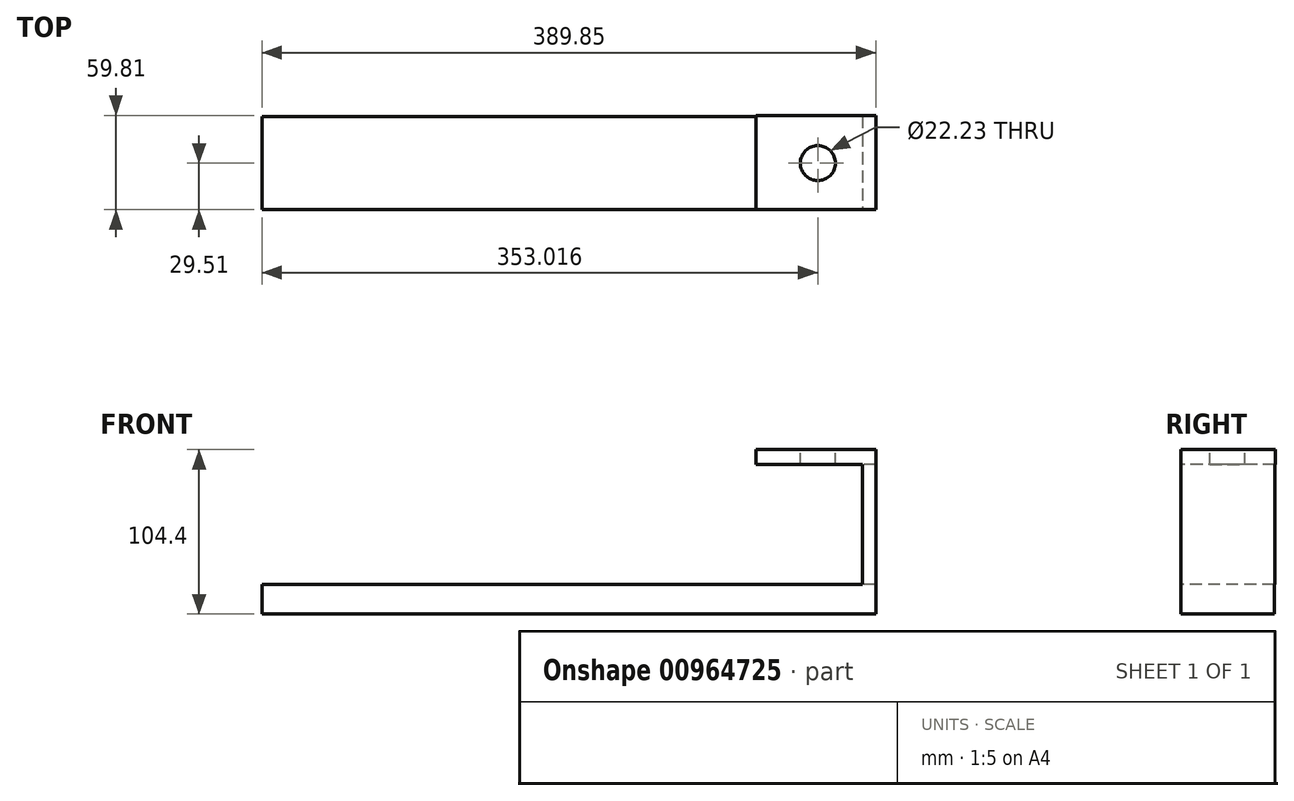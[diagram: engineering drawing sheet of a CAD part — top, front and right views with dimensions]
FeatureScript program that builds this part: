
annotation { "Feature Type Name" : "Feature", "Feature Type Description" : "" }
export const myFeature = defineFeature(function(context is Context, id is Id, definition is map)
    precondition{}
    {
        {
            var Q0;
            Q0=qCreatedBy(makeId("Top.planeOp"),FACE);
            var sketch = newSketch(context, id + "F0", { "sketchPlane" : qUnion([Q0])});
            skLineSegment(sketch, "E0.bottom", {"start": v(62.98, 23.22) * mm, "end": v(-13.26, 23.22) * mm});
            skLineSegment(sketch, "E0.top", {"start": v(62.98, -36.6) * mm, "end": v(-13.26, -36.6) * mm});
            skLineSegment(sketch, "E0.left", {"start": v(62.98, 23.22) * mm, "end": v(62.98, -36.6) * mm});
            skLineSegment(sketch, "E0.right", {"start": v(-13.26, 23.22) * mm, "end": v(-13.26, -36.6) * mm});
            skSolve(sketch);
        }
        {
            var Q0;
            Q0=makeQuery(id+"F0.imprint","IMPRINT",FACE,{"disambiguationData":[TD([[makeQuery(id+"F0.imprint","IMPRINT",EDGE,{"derivedFrom":sQuery(id+"F0.wireOp",EDGE,"E0.bottom")}),1.0]])]});
            extrude(context, id + "F1", {"entities" : qUnion([Q0]), "oppositeDirection" : true, "depth" : 9.52 * mm, "offsetDistance" : 25.4 * mm});
        }
        {
            var Q0;
            Q0=makeQuery(id+"F1.opExtrude","SWEPT_FACE",FACE,{"disambiguationData":[OSD([sQuery(id+"F0.wireOp",EDGE,"E0.top")])]});
            var sketch = newSketch(context, id + "F2", { "sketchPlane" : qUnion([Q0])});
            skLineSegment(sketch, "E1.bottom", {"start": v(62.98, -9.53) * mm, "end": v(54.4, -9.53) * mm});
            skLineSegment(sketch, "E1.top", {"start": v(62.98, -85.47) * mm, "end": v(54.4, -85.47) * mm});
            skLineSegment(sketch, "E1.left", {"start": v(62.98, -9.52) * mm, "end": v(62.98, -85.47) * mm});
            skLineSegment(sketch, "E1.right", {"start": v(54.4, -9.52) * mm, "end": v(54.4, -85.47) * mm});
            skSolve(sketch);
        }
        {
            var Q0;
            Q0 = qSketchRegion(id + "F2", true);
            extrude(context, id + "F3", {"entities" : qUnion([Q0]), "operationType" : NewBodyOperationType.ADD, "oppositeDirection" : true, "depth" : 59.44 * mm, "offsetDistance" : 25.4 * mm});
        }
        {
            var Q0;
            Q0=makeQuery(id+"F3.boolean.opBoolean","MERGE",FACE,{"derivedFrom":[makeQuery(id+"F1.opExtrude","SWEPT_FACE",FACE,{"disambiguationData":[OSD([sQuery(id+"F0.wireOp",EDGE,"E0.top")])]}),makeQuery(id+"F3.opExtrude","CAP_FACE",FACE,{"disambiguationData":[OSD([sQuery(id+"F2.wireOp",EDGE,"E1.bottom"),sQuery(id+"F2.wireOp",EDGE,"E1.top"),sQuery(id+"F2.wireOp",EDGE,"E1.left"),sQuery(id+"F2.wireOp",EDGE,"E1.right")])],"isStart":true})]});
            var sketch = newSketch(context, id + "F4", { "sketchPlane" : qUnion([Q0])});
            skLineSegment(sketch, "E2.bottom", {"start": v(62.98, -85.47) * mm, "end": v(-326.87, -85.47) * mm});
            skLineSegment(sketch, "E2.top", {"start": v(62.98, -104.4) * mm, "end": v(-326.87, -104.4) * mm});
            skLineSegment(sketch, "E2.left", {"start": v(62.98, -85.47) * mm, "end": v(62.98, -104.4) * mm});
            skLineSegment(sketch, "E2.right", {"start": v(-326.87, -85.47) * mm, "end": v(-326.87, -104.4) * mm});
            skSolve(sketch);
        }
        {
            var Q0;
            Q0 = qSketchRegion(id + "F4", true);
            extrude(context, id + "F5", {"entities" : qUnion([Q0]), "operationType" : NewBodyOperationType.ADD, "oppositeDirection" : true, "depth" : 59.18 * mm, "offsetDistance" : 25.4 * mm});
        }
        {
            var Q0;
            Q0=makeQuery(id+"F1.opExtrude","CAP_FACE",FACE,{"disambiguationData":[OSD([sQuery(id+"F0.wireOp",EDGE,"E0.bottom"),sQuery(id+"F0.wireOp",EDGE,"E0.top"),sQuery(id+"F0.wireOp",EDGE,"E0.left"),sQuery(id+"F0.wireOp",EDGE,"E0.right")])],"isStart":false});
            var sketch = newSketch(context, id + "F6", { "sketchPlane" : qUnion([Q0])});
            skCircle(sketch, "E3", {"center": v(26.15, 7.08) * mm, "radius": 11.55 * mm});
            skSolve(sketch);
        }
        {
            var Q0;
            Q0=sQuery(id+"F6.wireOp",VERTEX,"E3.center");
            var Q1;
            Q1=makeQuery(id+"F1.opExtrude","SWEPT_BODY",BODY,{"disambiguationData":[OSD([sQuery(id+"F0.wireOp",EDGE,"E0.bottom"),sQuery(id+"F0.wireOp",EDGE,"E0.top"),sQuery(id+"F0.wireOp",EDGE,"E0.left"),sQuery(id+"F0.wireOp",EDGE,"E0.right")])]});
            hole(context, id + "F7", {"style" : HoleStyle.SIMPLE, "endStyle" : HoleEndStyle.THROUGH, "holeDiameter" : 22.22 * mm, "majorDiameter" : 6.35 * mm, "isTappedThrough" : true, "tappedDepth" : 12.7 * mm, "tapClearance" : 3, "locations" : qUnion([Q0]), "scope" : qUnion([Q1]), "startStyle" : HoleStartStyle.SKETCH});
        }
    });
